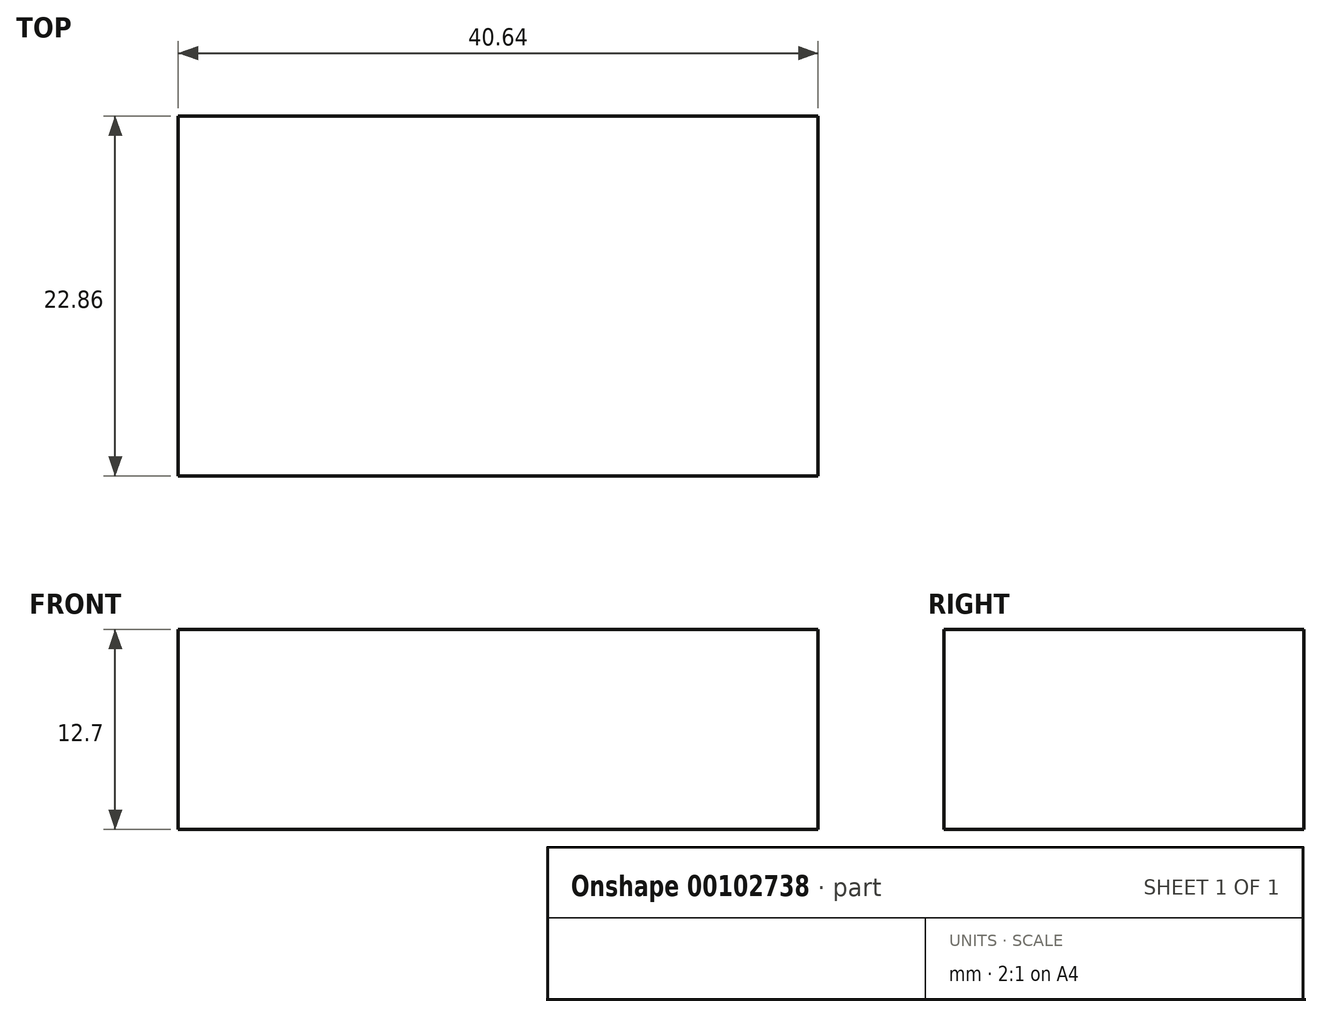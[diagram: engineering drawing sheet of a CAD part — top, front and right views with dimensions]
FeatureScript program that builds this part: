
annotation { "Feature Type Name" : "Feature", "Feature Type Description" : "" }
export const myFeature = defineFeature(function(context is Context, id is Id, definition is map)
    precondition{}
    {
        {
            var Q0;
            Q0=qCreatedBy(makeId("Top.planeOp"),FACE);
            var sketch = newSketch(context, id + "F0", { "sketchPlane" : qUnion([Q0])});
            skLineSegment(sketch, "E0.bottom", {"start": v(-27.41, 34.4) * mm, "end": v(13.23, 34.4) * mm});
            skLineSegment(sketch, "E0.top", {"start": v(-27.41, 11.54) * mm, "end": v(13.23, 11.54) * mm});
            skLineSegment(sketch, "E0.left", {"start": v(-27.41, 34.4) * mm, "end": v(-27.41, 11.54) * mm});
            skLineSegment(sketch, "E0.right", {"start": v(13.23, 34.4) * mm, "end": v(13.23, 11.54) * mm});
            skSolve(sketch);
        }
        {
            var Q0;
            Q0 = qSketchRegion(id + "F0", true);
            extrude(context, id + "F1", {"entities" : qUnion([Q0]), "depth" : 12.7 * mm});
        }
    });
